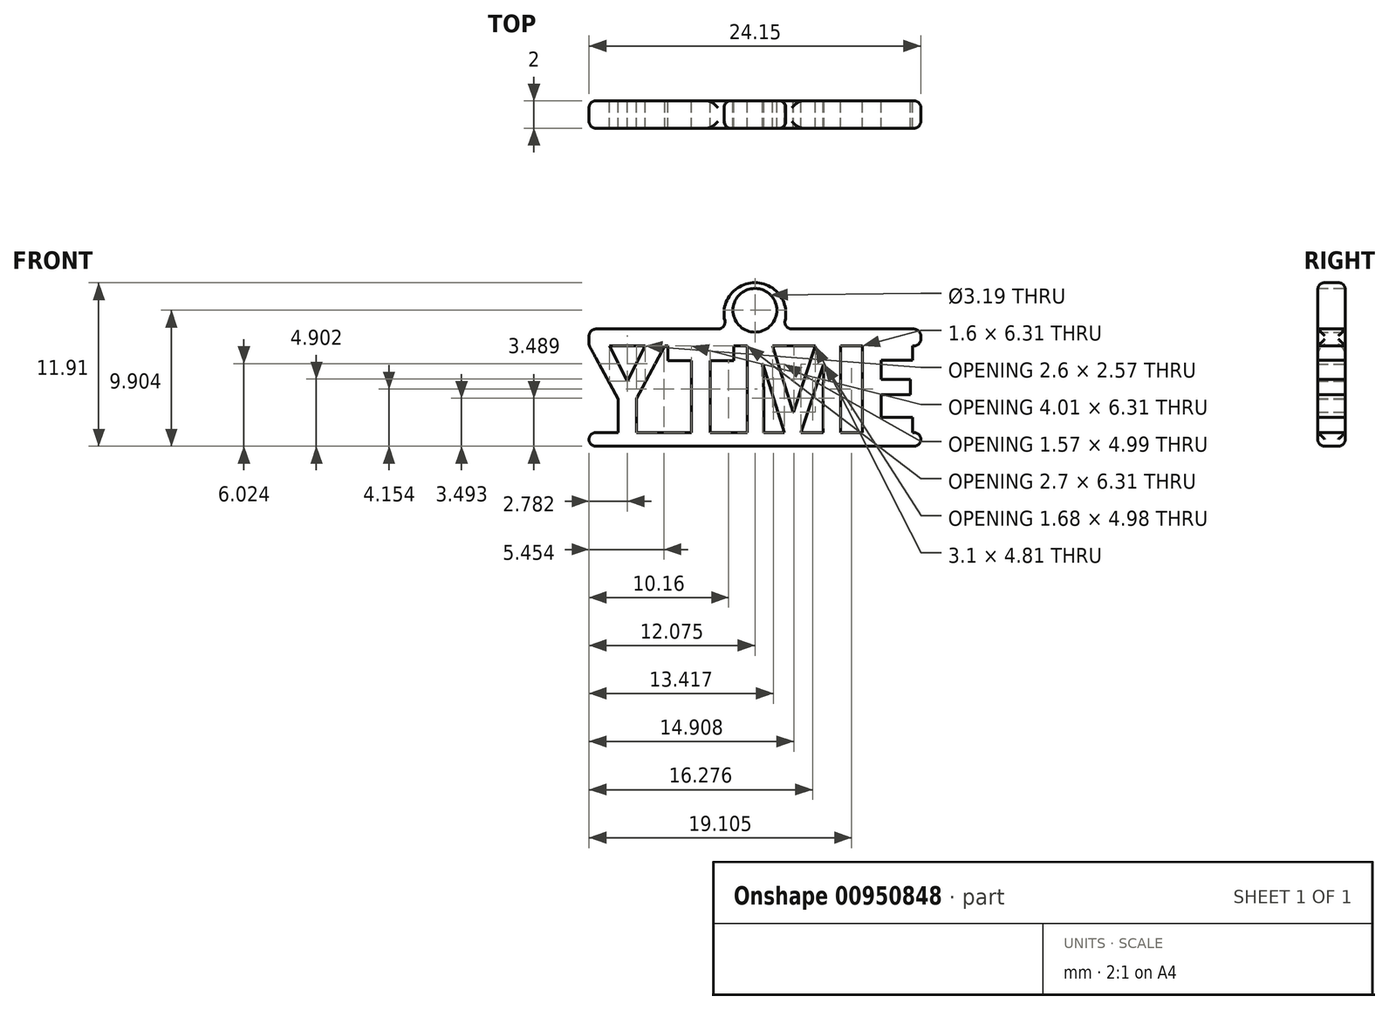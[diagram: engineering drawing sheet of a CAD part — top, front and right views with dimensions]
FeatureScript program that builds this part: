
annotation { "Feature Type Name" : "Feature", "Feature Type Description" : "" }
export const myFeature = defineFeature(function(context is Context, id is Id, definition is map)
    precondition{}
    {
        {
            var Q0;
            Q0=qCreatedBy(makeId("Front.planeOp"),FACE);
            var sketch = newSketch(context, id + "F0", { "sketchPlane" : qUnion([Q0])});
            skText(sketch, "E0", { "text": "YTME", "fontName": "OpenSans-Bold.ttf"});
            skLineSegment(sketch, "E1.bottom", {"start": v(0, 0) * mm, "end": v(24.15, 0) * mm});
            skLineSegment(sketch, "E1.top", {"start": v(0, -1) * mm, "end": v(24.15, -1) * mm});
            skLineSegment(sketch, "E1.left", {"start": v(0, 0) * mm, "end": v(0, -1) * mm});
            skLineSegment(sketch, "E1.right", {"start": v(24.15, 0) * mm, "end": v(24.15, -1) * mm});
            skLineSegment(sketch, "E2.bottom", {"start": v(0, 6.41) * mm, "end": v(24.15, 6.41) * mm});
            skLineSegment(sketch, "E2.top", {"start": v(0, 7.54) * mm, "end": v(24.15, 7.54) * mm});
            skLineSegment(sketch, "E2.left", {"start": v(0, 6.41) * mm, "end": v(0, 7.54) * mm});
            skLineSegment(sketch, "E2.right", {"start": v(24.15, 6.41) * mm, "end": v(24.15, 7.54) * mm});
            skArc(sketch, "E3", {"start": v(14.02, 7.54) * mm, "mid": v(12.08, 10.91) * mm, "end": v(10.13, 7.54) * mm});
            skLineSegment(sketch, "E4.top", {"start": v(0, 6.3) * mm, "end": v(24.15, 6.3) * mm});
            skLineSegment(sketch, "E4.left", {"start": v(0, 6.41) * mm, "end": v(0, 6.3) * mm});
            skLineSegment(sketch, "E4.right", {"start": v(24.15, 6.41) * mm, "end": v(24.15, 6.3) * mm});
            skPoint(sketch, "E5.center.orphan", {"position": v(12.08, 7.54) * mm});
            skCircle(sketch, "E6", {"center": v(12.08, 8.9) * mm, "radius": 1.6 * mm});
            const initialGuessF0  = {"E0": [0, 0, 1, 0, 0.00641]};
            skSetInitialGuess(sketch, initialGuessF0);
            skSolve(sketch);
        }
        {
            var Q0;
            Q0 = qSketchRegion(id + "F0", true);
            var Q1;
            {var subQ0=sQuery(id+"F0.wireOp",EDGE,"E0.sketch_text.stroke-13");Q1=makeQuery(id+"F0.imprint","IMPRINT",FACE,{"disambiguationData":[TD([[makeQuery(id+"F0.imprint","IMPRINT",EDGE,{"derivedFrom":subQ0}),-1.0]])]});}
            var Q2;
            {var subQ8=sQuery(id+"F0.wireOp",EDGE,"E0.sketch_text.stroke-10");Q2=makeQuery(id+"F0.imprint","IMPRINT",FACE,{"disambiguationData":[TD([[makeQuery(id+"F0.imprint","IMPRINT",EDGE,{"derivedFrom":subQ8}),-1.0]])]});}
            var Q3;
            {var subQ12=sQuery(id+"F0.wireOp",EDGE,"E0.sketch_text.stroke-17");Q3=makeQuery(id+"F0.imprint","IMPRINT",FACE,{"disambiguationData":[TD([[makeQuery(id+"F0.imprint","IMPRINT",EDGE,{"derivedFrom":subQ12}),-1.0]])]});}
            var Q4;
            {var subQ0=sQuery(id+"F0.wireOp",EDGE,"E0.sketch_text.stroke-23");Q4=makeQuery(id+"F0.imprint","IMPRINT",FACE,{"disambiguationData":[TD([[makeQuery(id+"F0.imprint","IMPRINT",EDGE,{"derivedFrom":subQ0}),-1.0]])]});}
            var Q5;
            {var subQ0=sQuery(id+"F0.wireOp",EDGE,"E0.sketch_text.stroke-27");Q5=makeQuery(id+"F0.imprint","IMPRINT",FACE,{"disambiguationData":[TD([[makeQuery(id+"F0.imprint","IMPRINT",EDGE,{"derivedFrom":subQ0}),-1.0]])]});}
            var Q6;
            {var subQ0=sQuery(id+"F0.wireOp",EDGE,"E0.sketch_text.stroke-1");Q6=makeQuery(id+"F0.imprint","IMPRINT",FACE,{"disambiguationData":[TD([[makeQuery(id+"F0.imprint","IMPRINT",EDGE,{"derivedFrom":subQ0}),-1.0]])]});}
            extrude(context, id + "F1", {"entities" : qUnion([Q0, Q1, Q2, Q3, Q4, Q5, Q6]), "depth" : 2 * mm, "offsetDistance" : 25 * mm});
        }
        {
            var Q0;
            Q0=makeQuery(id+"F1.opExtrude","SWEPT_FACE",FACE,{"disambiguationData":[OSD([sQuery(id+"F0.wireOp",EDGE,"E3")])]});
            var Q1;
            Q1=makeQuery(id+"F1.opExtrude","SWEPT_FACE",FACE,{"disambiguationData":[OSD([sQuery(id+"F0.wireOp",EDGE,"E1.top")])]});
            var Q2;
            Q2=makeQuery(id+"F1.opExtrude","SWEPT_FACE",FACE,{"disambiguationData":[OSD([sQuery(id+"F0.wireOp",EDGE,"E2.right"),sQuery(id+"F0.wireOp",EDGE,"E4.right")])]});
            var Q3;
            Q3=makeQuery(id+"F1.opExtrude","SWEPT_FACE",FACE,{"disambiguationData":[OSD([sQuery(id+"F0.wireOp",EDGE,"E1.right")])]});
            var Q4;
            Q4=makeQuery(id+"F1.opExtrude","SWEPT_FACE",FACE,{"disambiguationData":[OSD([sQuery(id+"F0.wireOp",EDGE,"E1.left")])]});
            var Q5;
            Q5=makeQuery(id+"F1.opExtrude","SWEPT_FACE",FACE,{"disambiguationData":[OSD([sQuery(id+"F0.wireOp",EDGE,"E2.left"),sQuery(id+"F0.wireOp",EDGE,"E4.left")])]});
            fillet(context, id + "F2", {"entities" : qUnion([Q0, Q1, Q2, Q3, Q4, Q5]), "radius" : .5 * mm, "tangentPropagation" : true, "allowEdgeOverflow" : false});
        }
    });
